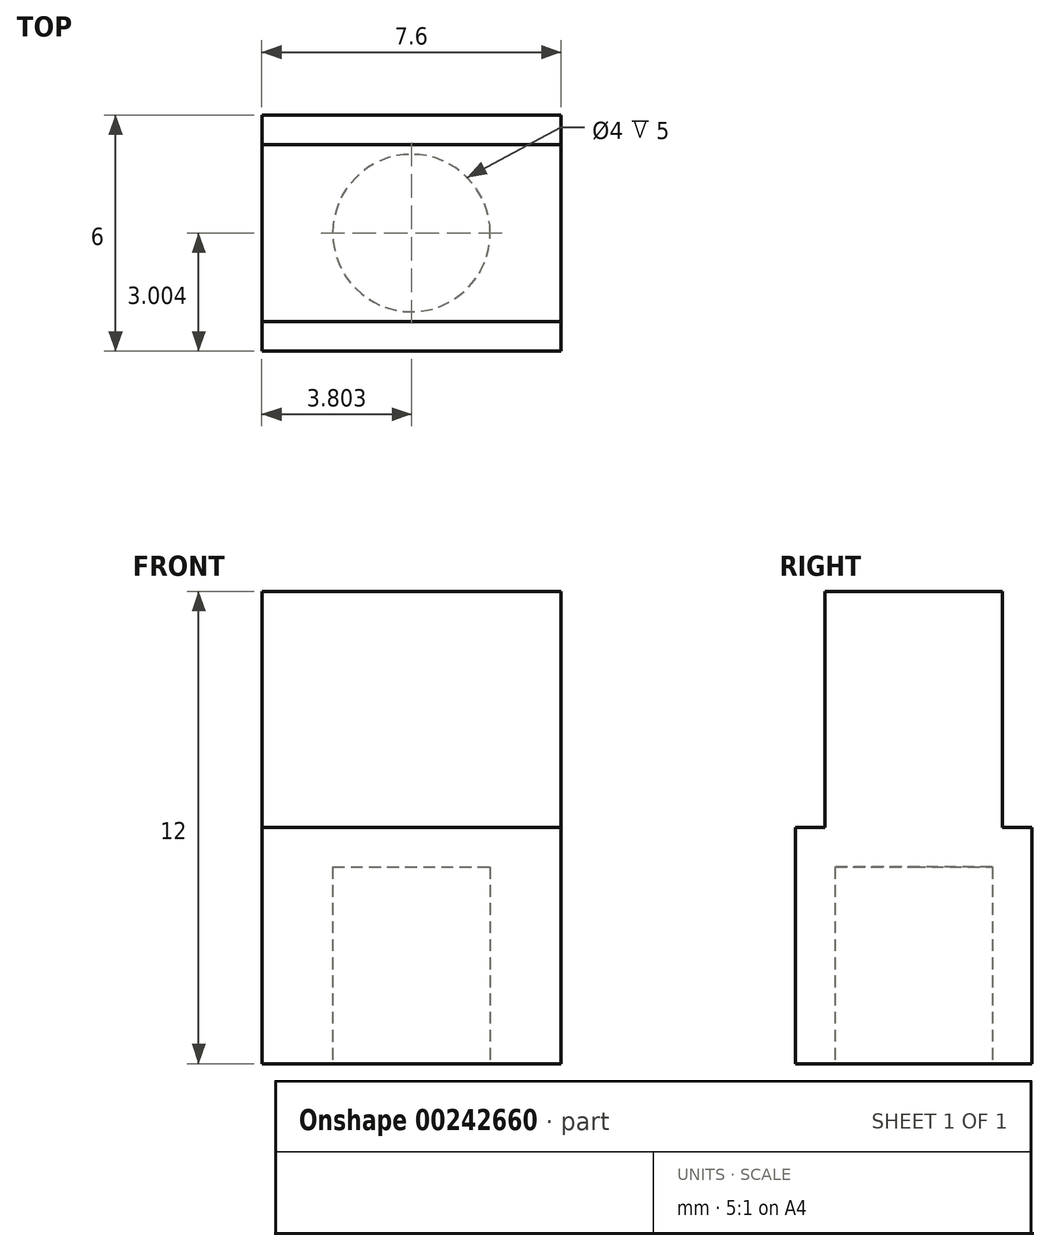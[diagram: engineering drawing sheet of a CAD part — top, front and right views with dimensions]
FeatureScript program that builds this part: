
annotation { "Feature Type Name" : "Feature", "Feature Type Description" : "" }
export const myFeature = defineFeature(function(context is Context, id is Id, definition is map)
    precondition{}
    {
        {
            var Q0;
            Q0=qCreatedBy(makeId("Top.planeOp"),FACE);
            var sketch = newSketch(context, id + "F0", { "sketchPlane" : qUnion([Q0])});
            skLineSegment(sketch, "E0.bottom", {"start": v(-54.47, 22.8) * mm, "end": v(-46.87, 22.8) * mm});
            skLineSegment(sketch, "E0.top", {"start": v(-54.47, 16.8) * mm, "end": v(-46.87, 16.8) * mm});
            skLineSegment(sketch, "E0.left", {"start": v(-54.47, 22.8) * mm, "end": v(-54.47, 16.8) * mm});
            skLineSegment(sketch, "E0.right", {"start": v(-46.87, 22.8) * mm, "end": v(-46.87, 16.8) * mm});
            skSolve(sketch);
        }
        {
            var Q0;
            Q0 = qSketchRegion(id + "F0", true);
            extrude(context, id + "F1", {"entities" : qUnion([Q0]), "depth" : 6 * mm});
        }
        {
            var Q0;
            Q0=makeQuery(id+"F1.opExtrude","CAP_FACE",FACE,{"disambiguationData":[OSD([sQuery(id+"F0.wireOp",EDGE,"E0.bottom"),sQuery(id+"F0.wireOp",EDGE,"E0.top"),sQuery(id+"F0.wireOp",EDGE,"E0.left"),sQuery(id+"F0.wireOp",EDGE,"E0.right")])],"isStart":false});
            var sketch = newSketch(context, id + "F2", { "sketchPlane" : qUnion([Q0])});
            skLineSegment(sketch, "E1.bottom", {"start": v(-54.47, 22.04) * mm, "end": v(-46.87, 22.04) * mm});
            skLineSegment(sketch, "E1.top", {"start": v(-54.47, 17.54) * mm, "end": v(-46.87, 17.54) * mm});
            skLineSegment(sketch, "E1.left", {"start": v(-54.47, 22.04) * mm, "end": v(-54.47, 17.54) * mm});
            skLineSegment(sketch, "E1.right", {"start": v(-46.87, 22.04) * mm, "end": v(-46.87, 17.54) * mm});
            skPoint(sketch, "E1.middle", {"position": v(-50.67, 19.8) * mm});
            skPoint(sketch, "E1.middle.positionSnap0", {"position": v(-54.47, 19.8) * mm});
            skPoint(sketch, "E1.middle.positionSnap1", {"position": v(-50.67, 22.8) * mm});
            skPoint(sketch, "E1.centerSnap0", {"position": v(-54.47, 19.8) * mm});
            skPoint(sketch, "E1.centerSnap1", {"position": v(-50.67, 22.8) * mm});
            skSolve(sketch);
        }
        {
            var Q0;
            Q0=makeQuery(id+"F2.imprint","IMPRINT",FACE,{"disambiguationData":[TD([[makeQuery(id+"F2.imprint","IMPRINT",EDGE,{"derivedFrom":sQuery(id+"F2.wireOp",EDGE,"E1.bottom")}),-1.0]])]});
            extrude(context, id + "F3", {"entities" : qUnion([Q0]), "operationType" : NewBodyOperationType.ADD, "depth" : 6 * mm});
        }
        {
            var Q0;
            Q0=makeQuery(id+"F1.opExtrude","CAP_FACE",FACE,{"disambiguationData":[OSD([sQuery(id+"F0.wireOp",EDGE,"E0.bottom"),sQuery(id+"F0.wireOp",EDGE,"E0.top"),sQuery(id+"F0.wireOp",EDGE,"E0.left"),sQuery(id+"F0.wireOp",EDGE,"E0.right")])],"isStart":true});
            var sketch = newSketch(context, id + "F4", { "sketchPlane" : qUnion([Q0])});
            skCircle(sketch, "E2", {"center": v(-50.67, -19.8) * mm, "radius": 2 * mm});
            skPoint(sketch, "E2.centerSnap0", {"position": v(-54.47, -19.8) * mm});
            skPoint(sketch, "E2.centerSnap1", {"position": v(-50.67, -16.8) * mm});
            skSolve(sketch);
        }
        {
            var Q0;
            Q0=makeQuery(id+"F4.imprint","IMPRINT",FACE,{"disambiguationData":[TD([[makeQuery(id+"F4.imprint","IMPRINT",EDGE,{"derivedFrom":sQuery(id+"F4.wireOp",EDGE,"E2")}),1.0]])]});
            extrude(context, id + "F5", {"entities" : qUnion([Q0]), "operationType" : NewBodyOperationType.REMOVE, "oppositeDirection" : true, "depth" : 5 * mm});
        }
    });
